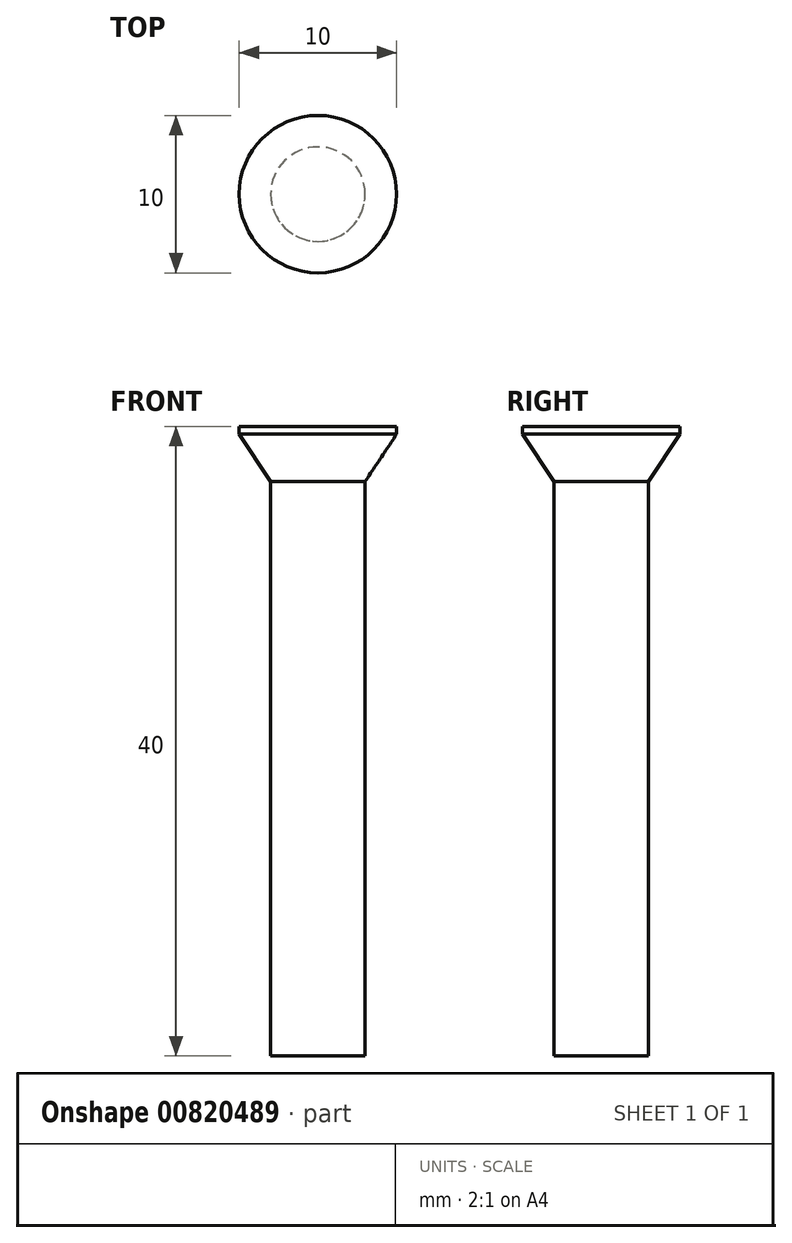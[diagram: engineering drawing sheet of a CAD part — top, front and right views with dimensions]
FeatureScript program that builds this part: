
annotation { "Feature Type Name" : "Feature", "Feature Type Description" : "" }
export const myFeature = defineFeature(function(context is Context, id is Id, definition is map)
    precondition{}
    {
        {
            var Q0;
            Q0=qCreatedBy(makeId("Top.planeOp"),FACE);
            var sketch = newSketch(context, id + "F0", { "sketchPlane" : qUnion([Q0])});
            skCircle(sketch, "E0", {"center": v(0, 0) * mm, "radius": 5 * mm});
            skSolve(sketch);
        }
        {
            var Q0;
            Q0 = qSketchRegion(id + "F0", true);
            var Q1;
            Q1=makeQuery(id+"F0.imprint","IMPRINT",FACE,{"disambiguationData":[TD([[makeQuery(id+"F0.imprint","IMPRINT",EDGE,{"derivedFrom":sQuery(id+"F0.wireOp",EDGE,"E0")}),1.0]])]});
            extrude(context, id + "F1", {"entities" : qUnion([Q0, Q1]), "depth" : 3.5 * mm, "offsetDistance" : 25 * mm});
        }
        {
            var Q0;
            Q0=makeQuery(id+"F1.opExtrude","CAP_FACE",FACE,{"disambiguationData":[OSD([sQuery(id+"F0.wireOp",EDGE,"E0")])],"isStart":true});
            var sketch = newSketch(context, id + "F2", { "sketchPlane" : qUnion([Q0])});
            skCircle(sketch, "E1", {"center": v(0, 0) * mm, "radius": 3 * mm});
            skSolve(sketch);
        }
        {
            var Q0;
            Q0=makeQuery(id+"F2.imprint","IMPRINT",FACE,{"disambiguationData":[TD([[makeQuery(id+"F2.imprint","IMPRINT",EDGE,{"derivedFrom":sQuery(id+"F2.wireOp",EDGE,"E1")}),1.0]])]});
            extrude(context, id + "F3", {"entities" : qUnion([Q0]), "operationType" : NewBodyOperationType.ADD, "depth" : (40 - 3.5) * mm, "offsetDistance" : 25 * mm});
        }
        {
            var Q0;
            Q0=makeQuery(id+"F1.opExtrude","CAP_EDGE",EDGE,{"disambiguationData":[OSD([sQuery(id+"F0.wireOp",EDGE,"E0")])],"isStart":true});
            chamfer(context, id + "F4", {"entities" : qUnion([Q0]), "chamferType" : ChamferType.TWO_OFFSETS, "width1" : 3 * mm, "oppositeDirection" : false, "width2" : 2 * mm, "tangentPropagation" : true});
        }
    });
